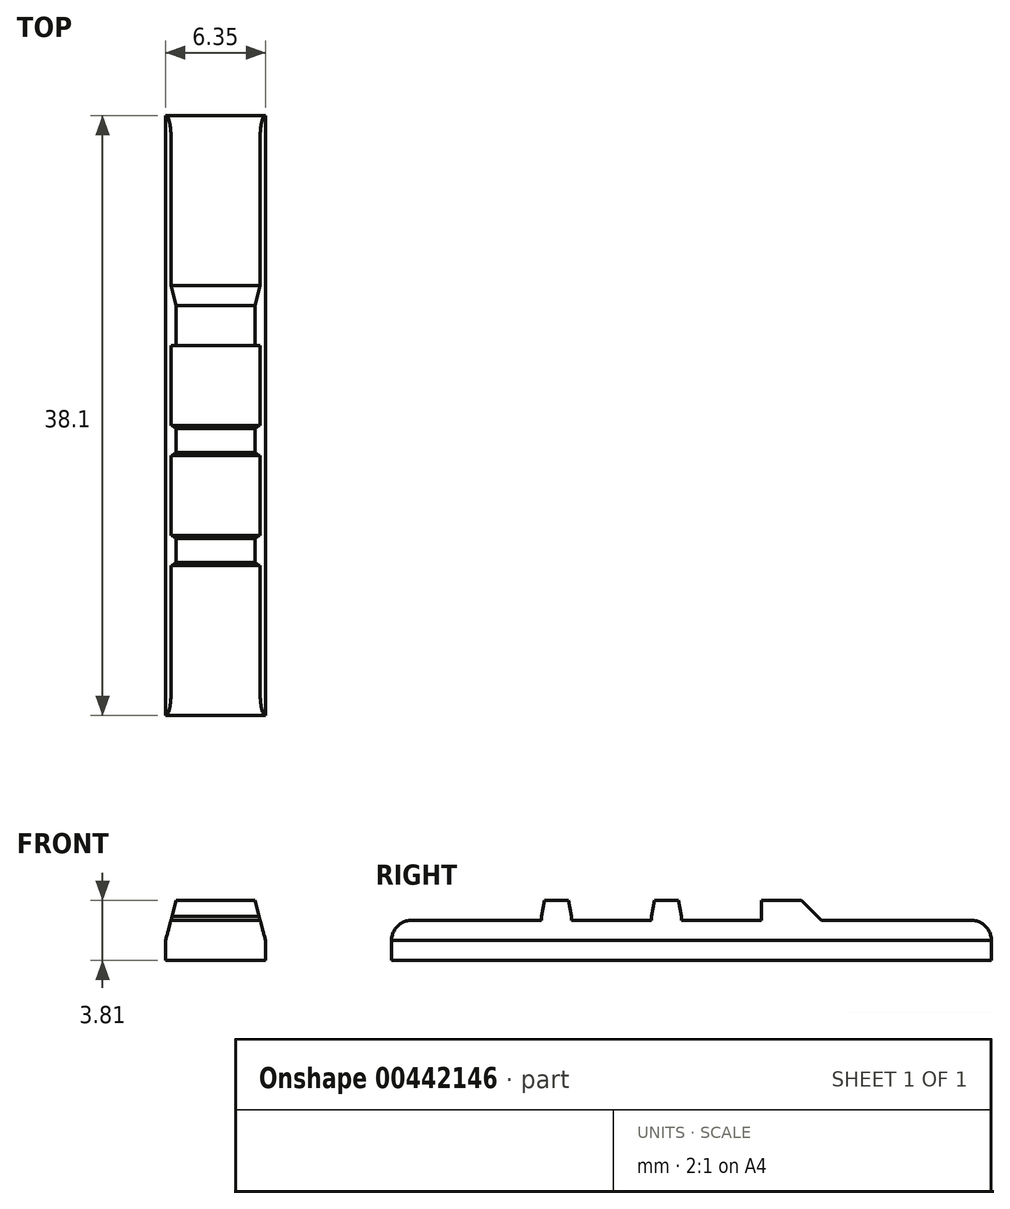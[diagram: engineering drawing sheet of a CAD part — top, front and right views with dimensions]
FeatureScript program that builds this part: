
annotation { "Feature Type Name" : "Feature", "Feature Type Description" : "" }
export const myFeature = defineFeature(function(context is Context, id is Id, definition is map)
    precondition{}
    {
        {
            var Q0;
            Q0=qCreatedBy(makeId("Right.planeOp"),FACE);
            var sketch = newSketch(context, id + "F0", { "sketchPlane" : qUnion([Q0])});
            skLineSegment(sketch, "E0", {"start": v(0, 0) * mm, "end": v(0, 1.27) * mm});
            skLineSegment(sketch, "E1", {"start": v(1.27, 2.54) * mm, "end": v(9.52, 2.54) * mm});
            skLineSegment(sketch, "E2", {"start": v(9.52, 2.54) * mm, "end": v(9.52, 3.81) * mm});
            skLineSegment(sketch, "E3", {"start": v(9.52, 3.81) * mm, "end": v(11.43, 3.81) * mm});
            skLineSegment(sketch, "E4", {"start": v(11.43, 3.8) * mm, "end": v(11.43, 2.54) * mm});
            skLineSegment(sketch, "E5", {"start": v(11.43, 2.54) * mm, "end": v(16.51, 2.54) * mm});
            skLineSegment(sketch, "E6", {"start": v(16.51, 2.54) * mm, "end": v(16.51, 3.8) * mm});
            skLineSegment(sketch, "E7", {"start": v(16.51, 3.8) * mm, "end": v(18.41, 3.8) * mm});
            skLineSegment(sketch, "E8", {"start": v(18.41, 3.8) * mm, "end": v(18.41, 2.54) * mm});
            skLineSegment(sketch, "E9", {"start": v(18.41, 2.54) * mm, "end": v(23.5, 2.54) * mm});
            skLineSegment(sketch, "E10", {"start": v(23.5, 2.54) * mm, "end": v(23.5, 3.8) * mm});
            skLineSegment(sketch, "E11", {"start": v(23.5, 3.8) * mm, "end": v(28.58, 3.8) * mm});
            skLineSegment(sketch, "E12", {"start": v(28.58, 3.8) * mm, "end": v(28.58, 2.54) * mm});
            skLineSegment(sketch, "E13", {"start": v(28.58, 2.54) * mm, "end": v(36.83, 2.54) * mm});
            skLineSegment(sketch, "E14", {"start": v(38.1, 1.27) * mm, "end": v(38.1, 0) * mm});
            skLineSegment(sketch, "E15", {"start": v(38.1, 0) * mm, "end": v(0, 0) * mm});
            skPoint(sketch, "E16.visualSharp", {"position": v(0, 2.54) * mm});
            skArc(sketch, "E16.filletArc", {"start": v(1.27, 2.54) * mm, "mid": v(0.37, 2.17) * mm, "end": v(0, 1.27) * mm});
            skPoint(sketch, "E17.visualSharp", {"position": v(38.1, 2.54) * mm});
            skArc(sketch, "E17.filletArc", {"start": v(38.1, 1.27) * mm, "mid": v(37.73, 2.17) * mm, "end": v(36.83, 2.54) * mm});
            skSolve(sketch);
        }
        {
            var Q0;
            Q0 = qSketchRegion(id + "F0", true);
            extrude(context, id + "F1", {"entities" : qUnion([Q0]), "depth" : 6.35 * mm});
        }
        {
            var Q0;
            Q0=makeQuery(id+"F1.opExtrude","SWEPT_EDGE",EDGE,{"disambiguationData":[OSD([sQuery(id+"F0.wireOp",EDGE,"E3"),sQuery(id+"F0.wireOp",EDGE,"E4")])]});
            var Q1;
            Q1=makeQuery(id+"F1.opExtrude","SWEPT_EDGE",EDGE,{"disambiguationData":[OSD([sQuery(id+"F0.wireOp",EDGE,"E2"),sQuery(id+"F0.wireOp",EDGE,"E3")])]});
            var Q2;
            Q2=makeQuery(id+"F1.opExtrude","SWEPT_EDGE",EDGE,{"disambiguationData":[OSD([sQuery(id+"F0.wireOp",EDGE,"E7"),sQuery(id+"F0.wireOp",EDGE,"E8")])]});
            chamfer(context, id + "F2", {"entities" : qUnion([Q0, Q1, Q2]), "chamferType" : ChamferType.OFFSET_ANGLE, "width" : 1.02 * mm, "oppositeDirection" : true, "angle" : 10 * degree, "tangentPropagation" : true});
        }
        {
            var Q0;
            Q0=makeQuery(id+"F1.opExtrude","SWEPT_EDGE",EDGE,{"disambiguationData":[OSD([sQuery(id+"F0.wireOp",EDGE,"E6"),sQuery(id+"F0.wireOp",EDGE,"E7")])]});
            chamfer(context, id + "F3", {"entities" : qUnion([Q0]), "chamferType" : ChamferType.OFFSET_ANGLE, "width" : 1.02 * mm, "oppositeDirection" : false, "angle" : 10 * degree, "tangentPropagation" : true});
        }
        {
            var Q0;
            Q0=makeQuery(id+"F1.opExtrude","CAP_EDGE",EDGE,{"disambiguationData":[OSD([sQuery(id+"F0.wireOp",EDGE,"E3")])],"isStart":false});
            chamfer(context, id + "F4", {"entities" : qUnion([Q0]), "chamferType" : ChamferType.OFFSET_ANGLE, "width" : 2.54 * mm, "oppositeDirection" : true, "angle" : 15 * degree, "tangentPropagation" : true});
        }
        {
            var Q0;
            Q0=makeQuery(id+"F1.opExtrude","CAP_EDGE",EDGE,{"disambiguationData":[OSD([sQuery(id+"F0.wireOp",EDGE,"E7")])],"isStart":true});
            chamfer(context, id + "F5", {"entities" : qUnion([Q0]), "chamferType" : ChamferType.OFFSET_ANGLE, "width" : 2.54 * mm, "oppositeDirection" : false, "angle" : 15 * degree, "tangentPropagation" : true});
        }
        {
            var Q0;
            Q0=makeQuery(id+"F1.opExtrude","SWEPT_EDGE",EDGE,{"disambiguationData":[OSD([sQuery(id+"F0.wireOp",EDGE,"E11"),sQuery(id+"F0.wireOp",EDGE,"E12")])]});
            chamfer(context, id + "F6", {"entities" : qUnion([Q0]), "width" : 2.54 * mm, "tangentPropagation" : true});
        }
    });
